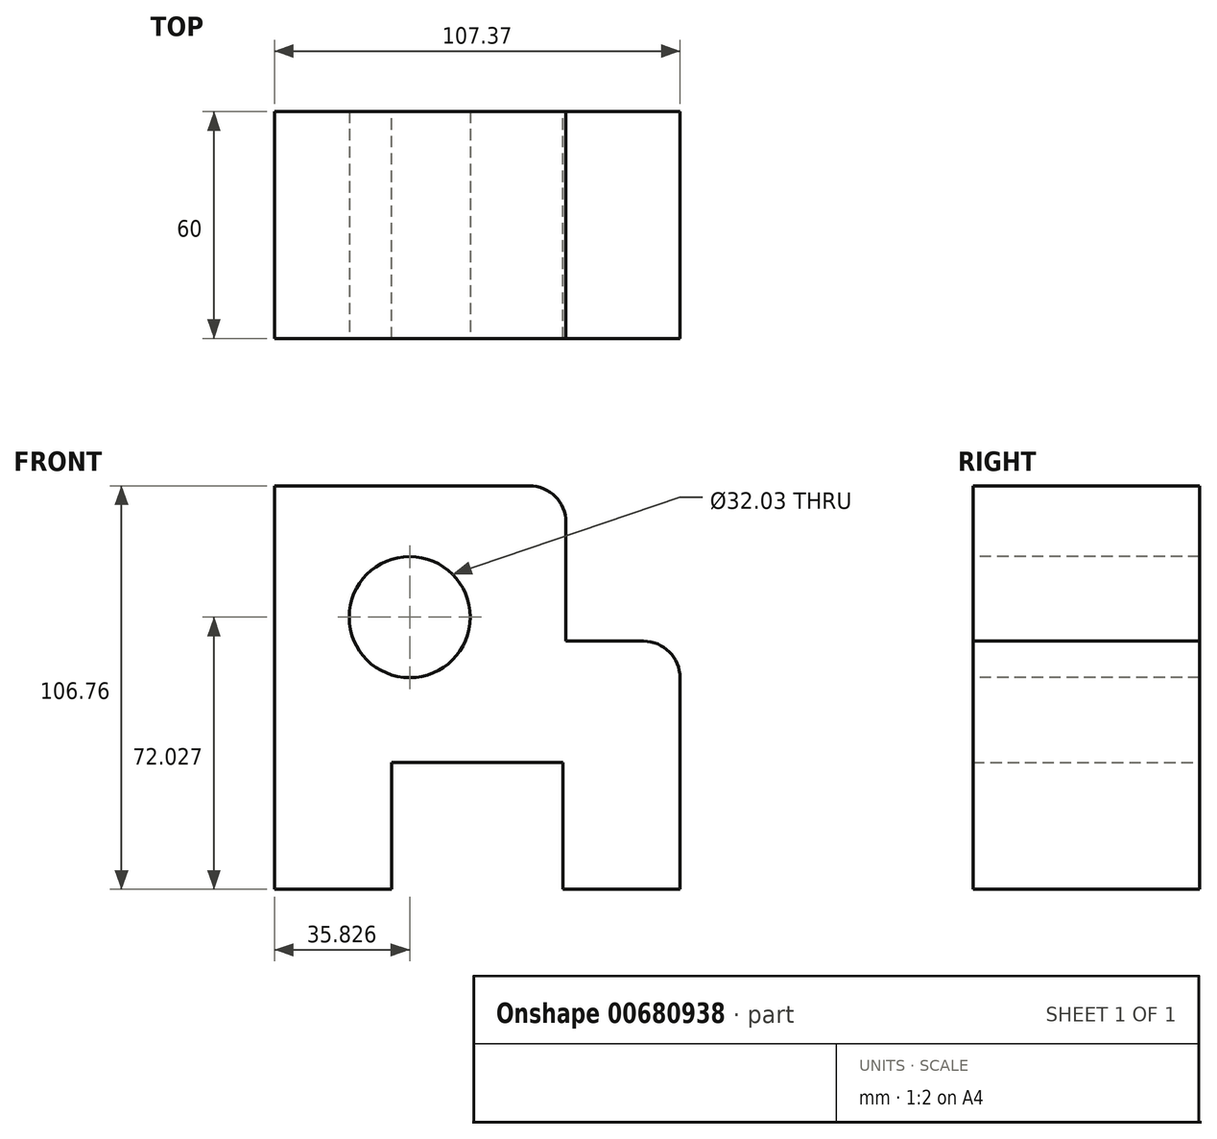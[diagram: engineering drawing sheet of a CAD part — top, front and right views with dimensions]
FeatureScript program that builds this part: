
annotation { "Feature Type Name" : "Feature", "Feature Type Description" : "" }
export const myFeature = defineFeature(function(context is Context, id is Id, definition is map)
    precondition{}
    {
        {
            var Q0;
            Q0=qCreatedBy(makeId("Front.planeOp"),FACE);
            var sketch = newSketch(context, id + "F0", { "sketchPlane" : qUnion([Q0])});
            skLineSegment(sketch, "E0", {"start": v(-58.95, 60.06) * mm, "end": v(18.22, 60.06) * mm});
            skLineSegment(sketch, "E1", {"start": v(18.22, 60.06) * mm, "end": v(18.22, 18.96) * mm});
            skLineSegment(sketch, "E2", {"start": v(18.22, 18.96) * mm, "end": v(48.42, 18.96) * mm});
            skLineSegment(sketch, "E3", {"start": v(48.42, 18.96) * mm, "end": v(48.42, -46.7) * mm});
            skLineSegment(sketch, "E4", {"start": v(48.42, -46.7) * mm, "end": v(17.38, -46.7) * mm});
            skLineSegment(sketch, "E5", {"start": v(17.38, -46.7) * mm, "end": v(17.38, -13.15) * mm});
            skLineSegment(sketch, "E6", {"start": v(17.38, -13.15) * mm, "end": v(-27.91, -13.15) * mm});
            skLineSegment(sketch, "E7", {"start": v(-27.91, -13.15) * mm, "end": v(-27.91, -46.7) * mm});
            skLineSegment(sketch, "E8", {"start": v(-27.91, -46.7) * mm, "end": v(-58.95, -46.7) * mm});
            skLineSegment(sketch, "E9", {"start": v(-58.95, -46.7) * mm, "end": v(-58.95, 60.06) * mm});
            skSolve(sketch);
        }
        {
            var Q0;
            Q0=makeQuery(id+"F0.imprint","IMPRINT",FACE,{"disambiguationData":[TD([[makeQuery(id+"F0.imprint","IMPRINT",EDGE,{"derivedFrom":sQuery(id+"F0.wireOp",EDGE,"E0")}),-1.0]])]});
            extrude(context, id + "F1", {"entities" : qUnion([Q0]), "depth" : 60 * mm, "offsetDistance" : 25 * mm});
        }
        {
            var Q0;
            Q0=makeQuery(id+"F1.opExtrude","SWEPT_EDGE",EDGE,{"disambiguationData":[OSD([sQuery(id+"F0.wireOp",EDGE,"E0"),sQuery(id+"F0.wireOp",EDGE,"E1")])]});
            var Q1;
            Q1=makeQuery(id+"F1.opExtrude","SWEPT_EDGE",EDGE,{"disambiguationData":[OSD([sQuery(id+"F0.wireOp",EDGE,"E2"),sQuery(id+"F0.wireOp",EDGE,"E3")])]});
            fillet(context, id + "F2", {"entities" : qUnion([Q0, Q1]), "radius" : 9.66 * mm, "tangentPropagation" : true, "allowEdgeOverflow" : false});
        }
        {
            var Q0;
            Q0=makeQuery(id+"F1.opExtrude","CAP_FACE",FACE,{"disambiguationData":[OSD([sQuery(id+"F0.wireOp",EDGE,"E0"),sQuery(id+"F0.wireOp",EDGE,"E1"),sQuery(id+"F0.wireOp",EDGE,"E2"),sQuery(id+"F0.wireOp",EDGE,"E3"),sQuery(id+"F0.wireOp",EDGE,"E4"),sQuery(id+"F0.wireOp",EDGE,"E5"),sQuery(id+"F0.wireOp",EDGE,"E6"),sQuery(id+"F0.wireOp",EDGE,"E7"),sQuery(id+"F0.wireOp",EDGE,"E8"),sQuery(id+"F0.wireOp",EDGE,"E9")])],"isStart":false});
            var sketch = newSketch(context, id + "F3", { "sketchPlane" : qUnion([Q0])});
            skCircle(sketch, "E10", {"center": v(-23.12, 25.33) * mm, "radius": 16.01 * mm});
            skLineSegment(sketch, "E11", {"start": v(-39.14, 25.23) * mm, "end": v(-39.34, 60.06) * mm, "construction": true});
            skSolve(sketch);
        }
        {
            var Q0;
            Q0=makeQuery(id+"F3.imprint","IMPRINT",FACE,{"disambiguationData":[TD([[makeQuery(id+"F3.imprint","IMPRINT",EDGE,{"derivedFrom":sQuery(id+"F3.wireOp",EDGE,"E10")}),1.0]])]});
            extrude(context, id + "F4", {"entities" : qUnion([Q0]), "operationType" : NewBodyOperationType.REMOVE, "oppositeDirection" : true, "depth" : 101 * mm, "offsetDistance" : 25 * mm});
        }
    });
